# Revit family: Haworth_BuzziFree_Screen
name_source: partatom
category: Furniture
revit_build: Autodesk Revit 2018 (Build: 20170223_1515(x64)
units: mm (PartAtom-declared; Revit-internal decimal feet)

## family parameters
Always vertical = Yes
Cut with Voids When Loaded = No
OmniClass Number = 23.40.20.00
OmniClass Title = General Furniture and Specialties
Room Calculation Point = No
Shared = No
Work Plane-Based = No

## types (4) — shared parameters
Actual Depth = 19.29 "
Arc Radius = 3.313 "
Assembly Code = E2020200
Base Width = 29.13 "
Custom Size = No
Manufacturer = Haworth
Model = HCBZ-FES
Revision = 1
Size = Verify Final Dim. w/ Haworth
Standard Depth = 19.29 in.
Standard Height = 47.25, 55, 63, 71 in.
Standard Width = 31.5, 39.5, 47.25, 55.25, 63, 71, 78.75 in.
URL = http://www.haworth.com
URL - Product = https://www.haworth.com
Warranty = http://www.haworth.com

## per-type parameters (varying)
| type | Actual Height | Actual Width | Description |
| HCBZ-FES - 47.25h 78.75w | 47.25 " | 78.75 " | Haworth BuzziFree Screen 47.25h 78.75w |
| HCBZ-FES - 55h 78.75w | 55 " | 78.75 " | Haworth BuzziFree Screen 55h 78.75w |
| HCBZ-FES - 63h 71w | 63 " | 71 " | Haworth BuzziFree Screen 63h 71w |
| HCBZ-FES - 71h 63w | 71 " | 63 " | Haworth BuzziFree Screen 71h 63w |

## geometry (parser evidence)
native form markers: Sweep x2
no freeform markers — native parametric forms only
